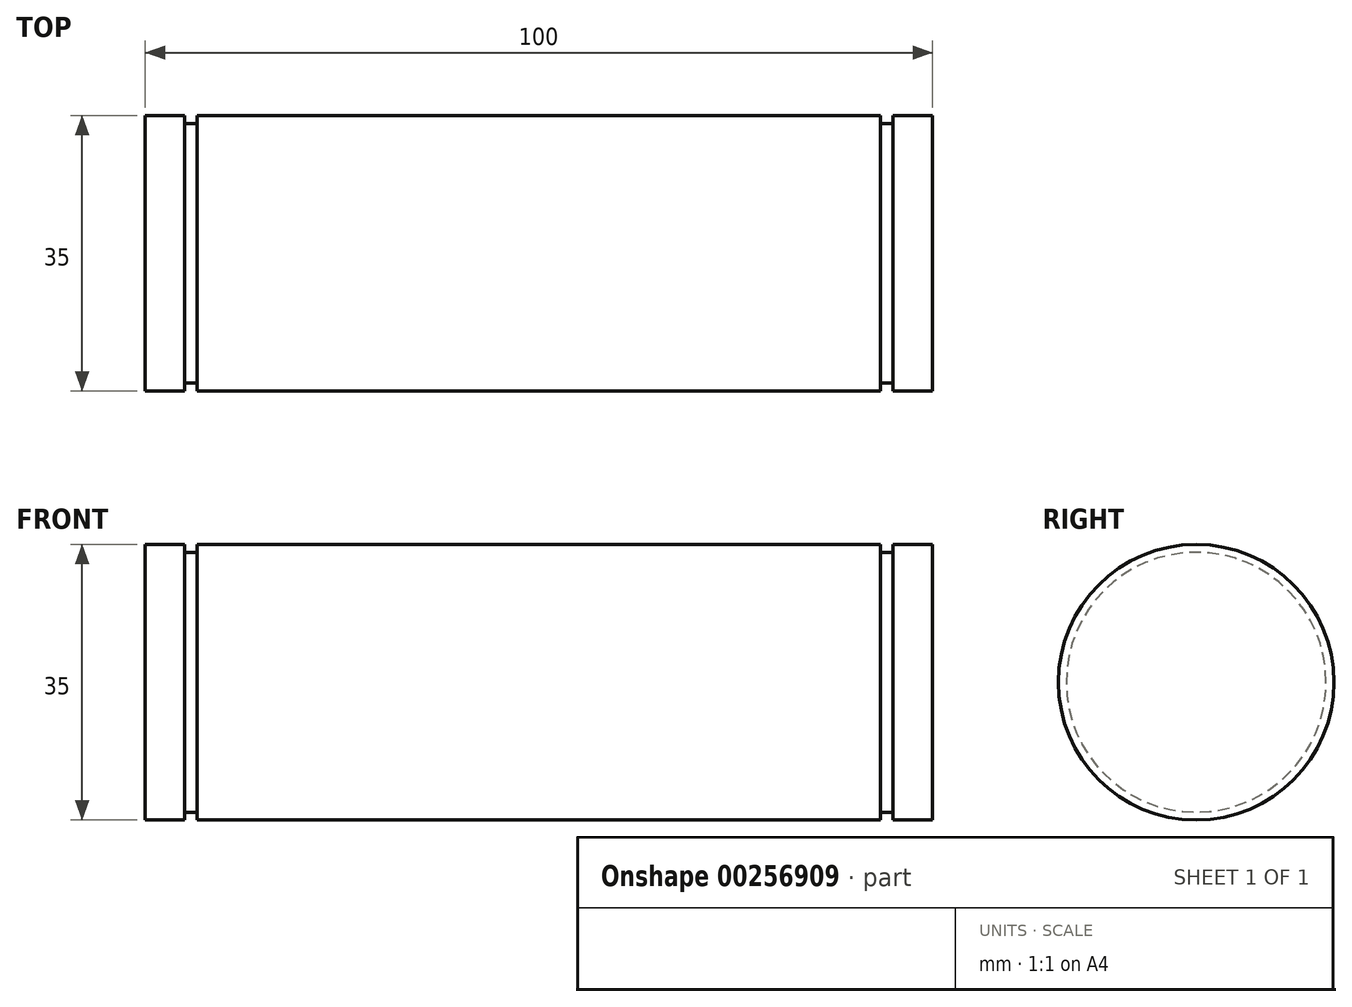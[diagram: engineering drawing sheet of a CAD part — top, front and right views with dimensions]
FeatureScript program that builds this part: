
annotation { "Feature Type Name" : "Feature", "Feature Type Description" : "" }
export const myFeature = defineFeature(function(context is Context, id is Id, definition is map)
    precondition{}
    {
        {
            var Q0;
            Q0=qCreatedBy(makeId("Right.planeOp"),FACE);
            var sketch = newSketch(context, id + "F0", { "sketchPlane" : qUnion([Q0])});
            skCircle(sketch, "E0", {"center": v(0, 0) * mm, "radius": 17.5 * mm});
            skSolve(sketch);
        }
        {
            var Q0;
            Q0=makeQuery(id+"F0.imprint","IMPRINT",FACE,{"disambiguationData":[TD([[makeQuery(id+"F0.imprint","IMPRINT",EDGE,{"derivedFrom":sQuery(id+"F0.wireOp",EDGE,"E0")}),1.0]])]});
            extrude(context, id + "F1", {"entities" : qUnion([Q0]), "oppositeDirection" : true, "depth" : 100 * mm});
        }
        {
            var Q0;
            Q0=qCreatedBy(makeId("Front.planeOp"),FACE);
            var sketch = newSketch(context, id + "F2", { "sketchPlane" : qUnion([Q0])});
            skLineSegment(sketch, "E1", {"start": v(0, 0) * mm, "end": v(-100, 0) * mm, "construction": true});
            skLineSegment(sketch, "E2.bottom", {"start": v(-5, 17.5) * mm, "end": v(-6.6, 17.5) * mm});
            skLineSegment(sketch, "E2.top", {"start": v(-5, 16.5) * mm, "end": v(-6.6, 16.5) * mm});
            skLineSegment(sketch, "E2.left", {"start": v(-5, 17.5) * mm, "end": v(-5, 16.5) * mm});
            skLineSegment(sketch, "E2.right", {"start": v(-6.6, 17.5) * mm, "end": v(-6.6, 16.5) * mm});
            skLineSegment(sketch, "E3", {"start": v(-50, 0) * mm, "end": v(-50, 21.88) * mm, "construction": true});
            skPoint(sketch, "E3.endSnap0", {"position": v(-50, 0) * mm});
            skLineSegment(sketch, "E4.MirrorCS", {"start": v(-95, 17.5) * mm, "end": v(-93.4, 17.5) * mm});
            skLineSegment(sketch, "E5.MirrorCS", {"start": v(-95, 16.5) * mm, "end": v(-93.4, 16.5) * mm});
            skLineSegment(sketch, "E6.MirrorCS", {"start": v(-93.4, 17.5) * mm, "end": v(-93.4, 16.5) * mm});
            skLineSegment(sketch, "E7.MirrorCS", {"start": v(-95, 17.5) * mm, "end": v(-95, 16.5) * mm});
            skSolve(sketch);
        }
        {
            var Q0;
            Q0 = qSketchRegion(id + "F2", true);
            var Q1;
            Q1=sQuery(id+"F2.wireOp",EDGE,"E1");
            revolve(context, id + "F3", {"operationType" : NewBodyOperationType.REMOVE, "entities" : qUnion([Q0]), "axis" : qUnion([Q1]), "revolveType" : RevolveType.FULL, "oppositeDirection" : true});
        }
    });
